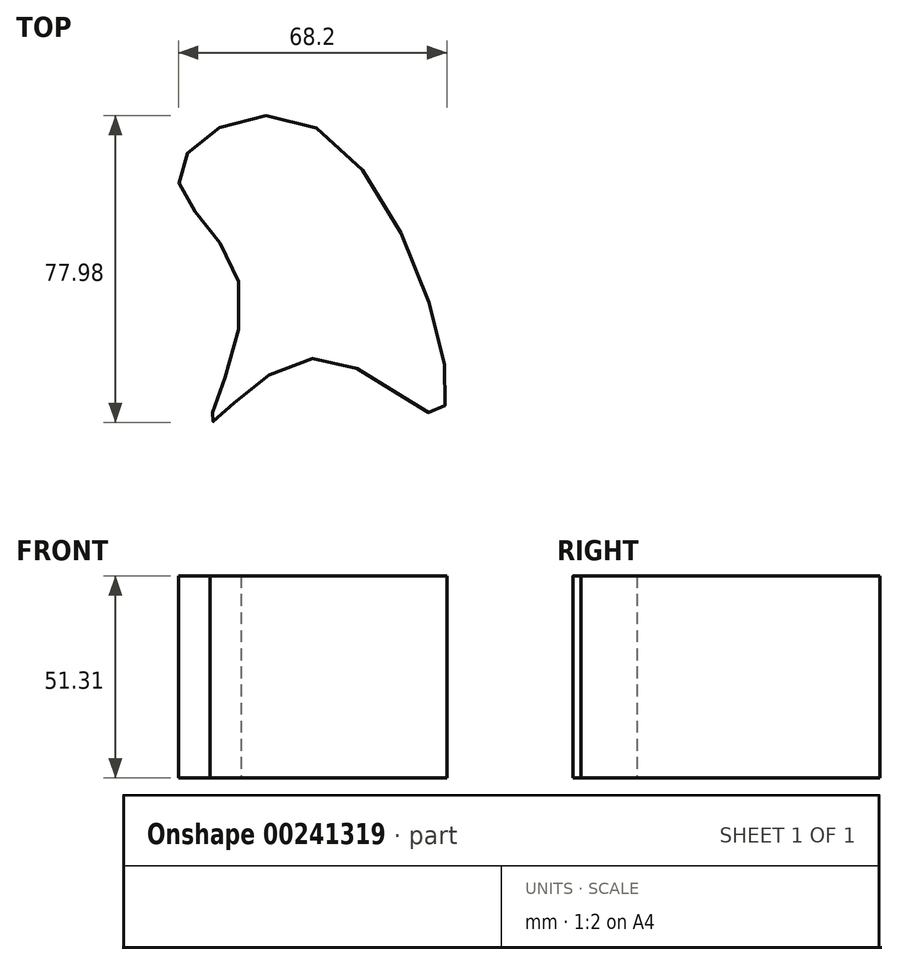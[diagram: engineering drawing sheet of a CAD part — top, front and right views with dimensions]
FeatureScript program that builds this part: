
annotation { "Feature Type Name" : "Feature", "Feature Type Description" : "" }
export const myFeature = defineFeature(function(context is Context, id is Id, definition is map)
    precondition{}
    {
        {
            var Q0;
            Q0=qCreatedBy(makeId("Top.planeOp"),FACE);
            var sketch = newSketch(context, id + "F0", { "sketchPlane" : qUnion([Q0])});
            skFitSpline(sketch, "E0", {"points": [v(0, 40.57) * mm, v(-35.01, 29.09) * mm, v(-19.45, 0) * mm, v(-26.86, -34.27) * mm, v(0, -17.97) * mm, v(31.68, -31.68) * mm, v(0, 40.57) * mm]});
            skSolve(sketch);
        }
        {
            var Q0;
            Q0=makeQuery(id+"F0.imprint","IMPRINT",FACE,{"disambiguationData":[TD([[makeQuery(id+"F0.imprint","IMPRINT",EDGE,{"derivedFrom":sQuery(id+"F0.wireOp",EDGE,"E0")}),1.0]])]});
            extrude(context, id + "F1", {"entities" : qUnion([Q0]), "depth" : 51.3 * mm});
        }
    });
